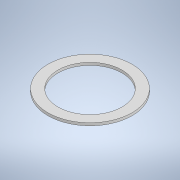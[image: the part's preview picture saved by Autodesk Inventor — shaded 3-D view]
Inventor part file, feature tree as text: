
AUTODESK INVENTOR PART (.ipt)
format: ipt  version: 2021 (Build 250183000, 183)  size: 99,840 bytes
history: native  units: mm
features: extrude x1, sketch x1
ambient origin geometry x8: Origin, YZ Plane, XZ Plane, XY Plane, X Axis, Y Axis, Z Axis, Center Point
bodies: Solid1 (feature_tree)
feature tree (2):
  extrude  "Extrusion1"  Depth=0.5mm
  sketch  "Sketch1"  dims[d0=16.0mm d1=12.2mm d2=0.5mm d3=0.0mm]
